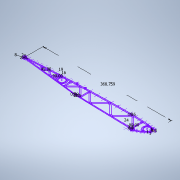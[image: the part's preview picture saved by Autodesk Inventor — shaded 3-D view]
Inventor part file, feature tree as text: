
AUTODESK INVENTOR PART (.ipt)
format: ipt  version: 2022 (Build 260153000, 153)  size: 265,728 bytes
history: native  units: mm
features: sketch x1
ambient origin geometry x8: Origin, YZ Plane, XZ Plane, XY Plane, X Axis, Y Axis, Z Axis, Center Point
feature tree (1):
  sketch  "Sketch1"  dims[d31=34.456mm d50=368.759386mm d57=16.0mm d69=8.0mm d80=19.0mm d81=16.0mm d82=1.0mm d83=1.0mm d84=1.0mm d85=1.0mm d86=1.0mm d87=0.8mm d88=1.0mm d90=19.0mm d94=5.0mm d95=5.0mm d105=5.0mm d106=5.0mm d108=2.0mm d114=5.0mm d115=5.0mm d116=24.0mm d117=2.5mm d118=2.5mm d123=2.5mm d124=2.5mm d125=10.0mm d126=24.0mm d127=24.0mm d128=27.0mm d135=0.5mm d139=7.0mm d169=27.0mm d181=45.0deg d185=7.0mm d186=45.0deg d190=7.0mm d191=45.0deg d206=90.0deg d212=90.0deg d215=7.0mm d216=90.0deg d219=7.0mm]
